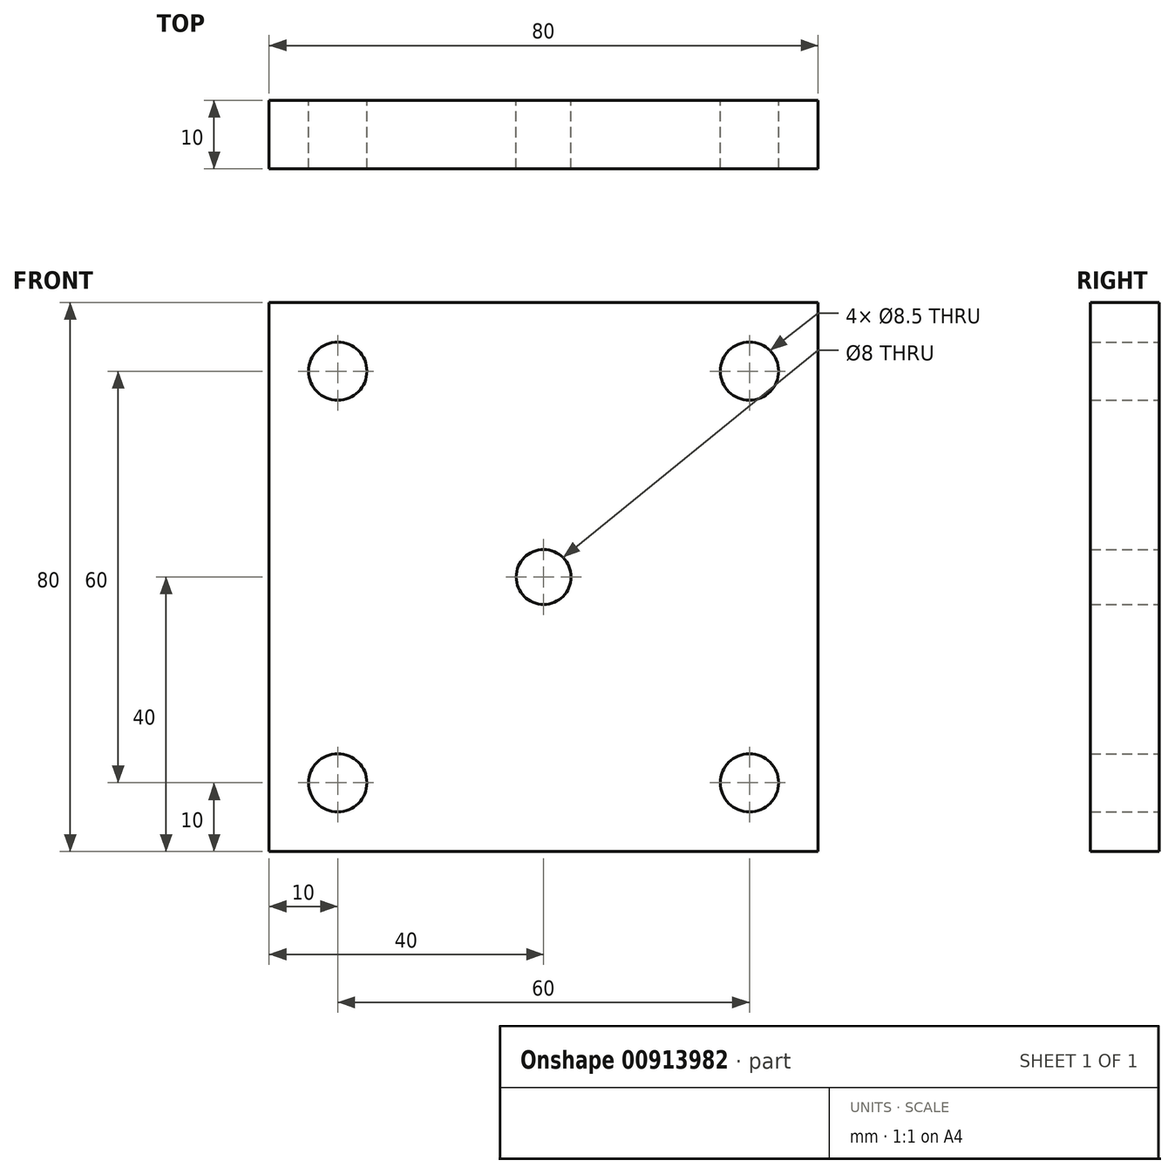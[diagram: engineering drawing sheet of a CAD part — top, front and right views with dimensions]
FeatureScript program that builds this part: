
annotation { "Feature Type Name" : "Feature", "Feature Type Description" : "" }
export const myFeature = defineFeature(function(context is Context, id is Id, definition is map)
    precondition{}
    {
        {
            var Q0;
            Q0=qCreatedBy(makeId("Front.planeOp"),FACE);
            var sketch = newSketch(context, id + "F0", { "sketchPlane" : qUnion([Q0])});
            skLineSegment(sketch, "E0.bottom", {"start": v(-40, 40) * mm, "end": v(40, 40) * mm});
            skLineSegment(sketch, "E0.top", {"start": v(-40, -40) * mm, "end": v(40, -40) * mm});
            skLineSegment(sketch, "E0.left", {"start": v(-40, 40) * mm, "end": v(-40, -40) * mm});
            skLineSegment(sketch, "E0.right", {"start": v(40, 40) * mm, "end": v(40, -40) * mm});
            skPoint(sketch, "E1", {"position": v(-30, 30) * mm});
            skPoint(sketch, "E2.0.1.0", {"position": v(-30, -30) * mm});
            skPoint(sketch, "E2.1.0.0", {"position": v(30, 30) * mm});
            skPoint(sketch, "E2.1.1.0", {"position": v(30, -30) * mm});
            skLineSegment(sketch, "E2.direction1", {"start": v(-30, 30) * mm, "end": v(30, 30) * mm, "construction": true});
            skLineSegment(sketch, "E2.direction2", {"start": v(-30, 30) * mm, "end": v(-30, -30) * mm, "construction": true});
            skSolve(sketch);
        }
        {
            var Q0;
            Q0 = qSketchRegion(id + "F0", true);
            extrude(context, id + "F1", {"entities" : qUnion([Q0]), "depth" : 10 * mm, "offsetDistance" : 25 * mm});
        }
        {
            var Q0;
            Q0=sQuery(id+"F0.wireOp",VERTEX,"E1");
            var Q1;
            Q1=sQuery(id+"F0.wireOp",VERTEX,"E2.1.0.0");
            var Q2;
            Q2=sQuery(id+"F0.wireOp",VERTEX,"E2.1.1.0");
            var Q3;
            Q3=sQuery(id+"F0.wireOp",VERTEX,"E2.0.1.0");
            var Q4;
            Q4=makeQuery(id+"F1.opExtrude","SWEPT_BODY",BODY,{"disambiguationData":[OSD([sQuery(id+"F0.wireOp",EDGE,"E0.bottom"),sQuery(id+"F0.wireOp",EDGE,"E0.top"),sQuery(id+"F0.wireOp",EDGE,"E0.left"),sQuery(id+"F0.wireOp",EDGE,"E0.right")])]});
            hole(context, id + "F2", {"style" : HoleStyle.SIMPLE, "endStyle" : HoleEndStyle.THROUGH, "oppositeDirection" : true, "holeDiameter" : 8.5 * mm, "majorDiameter" : 5 * mm, "isTappedThrough" : true, "tappedDepth" : 12 * mm, "tapClearance" : 3, "locations" : qUnion([Q0, Q1, Q2, Q3]), "scope" : qUnion([Q4])});
        }
        {
            var Q0;
            Q0=qCreatedBy(makeId("Front.planeOp"),FACE);
            var sketch = newSketch(context, id + "F3", { "sketchPlane" : qUnion([Q0])});
            skPoint(sketch, "E3", {"position": v(0, 0) * mm});
            skSolve(sketch);
        }
        {
            var Q0;
            Q0=sQuery(id+"F3.wireOp",VERTEX,"E3");
            var Q1;
            Q1=makeQuery(id+"F1.opExtrude","SWEPT_BODY",BODY,{"disambiguationData":[OSD([sQuery(id+"F0.wireOp",EDGE,"E0.bottom"),sQuery(id+"F0.wireOp",EDGE,"E0.top"),sQuery(id+"F0.wireOp",EDGE,"E0.left"),sQuery(id+"F0.wireOp",EDGE,"E0.right")])]});
            hole(context, id + "F4", {"style" : HoleStyle.SIMPLE, "endStyle" : HoleEndStyle.THROUGH, "oppositeDirection" : true, "holeDiameter" : 8 * mm, "majorDiameter" : 5 * mm, "isTappedThrough" : true, "tappedDepth" : 12 * mm, "tapClearance" : 3, "locations" : qUnion([Q0]), "scope" : qUnion([Q1])});
        }
    });
